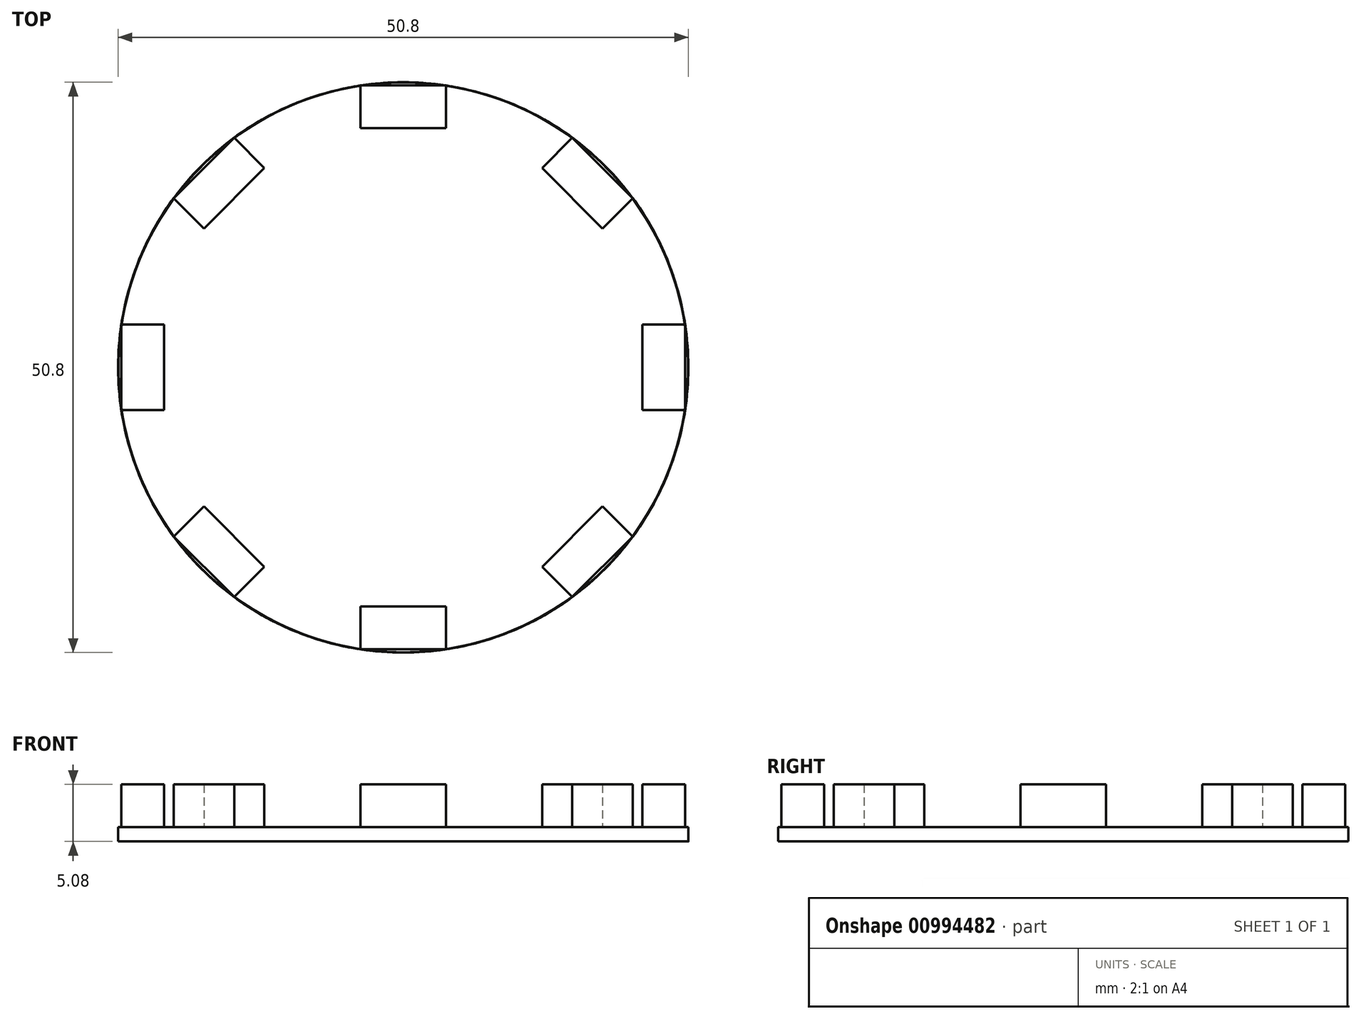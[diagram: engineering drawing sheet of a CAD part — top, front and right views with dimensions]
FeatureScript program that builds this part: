
annotation { "Feature Type Name" : "Feature", "Feature Type Description" : "" }
export const myFeature = defineFeature(function(context is Context, id is Id, definition is map)
    precondition{}
    {
        {
            var Q0;
            Q0=qCreatedBy(makeId("Top.planeOp"),FACE);
            var sketch = newSketch(context, id + "F0", { "sketchPlane" : qUnion([Q0])});
            skCircle(sketch, "E0", {"center": v(0, 0) * mm, "radius": 25.4 * mm});
            skSolve(sketch);
        }
        {
            var Q0;
            Q0 = qSketchRegion(id + "F0", true);
            extrude(context, id + "F1", {"entities" : qUnion([Q0]), "depth" : 1.27 * mm, "offsetDistance" : 25.4 * mm});
        }
        {
            var Q0;
            Q0=qCreatedBy(makeId("Top.planeOp"),FACE);
            var sketch = newSketch(context, id + "F2", { "sketchPlane" : qUnion([Q0])});
            skLineSegment(sketch, "E1.bottom", {"start": v(-25.11, 3.81) * mm, "end": v(-21.3, 3.81) * mm});
            skLineSegment(sketch, "E1.top", {"start": v(-25.11, -3.81) * mm, "end": v(-21.3, -3.81) * mm});
            skLineSegment(sketch, "E1.left", {"start": v(-25.11, 3.81) * mm, "end": v(-25.11, -3.81) * mm});
            skLineSegment(sketch, "E1.right", {"start": v(-21.3, 3.81) * mm, "end": v(-21.3, -3.81) * mm});
            skSolve(sketch);
        }
        {
            var Q0;
            Q0 = qSketchRegion(id + "F2", true);
            extrude(context, id + "F3", {"entities" : qUnion([Q0]), "operationType" : NewBodyOperationType.ADD, "depth" : 5.08 * mm, "offsetDistance" : 25.4 * mm});
        }
        {
            var Q0;
            Q0=makeQuery(id+"F1.opExtrude","SWEPT_BODY",BODY,{"disambiguationData":[OSD([sQuery(id+"F0.wireOp",EDGE,"E0")])]});
            var Q1;
            Q1=makeQuery(id+"F3.boolean.opBoolean","SPLIT",EDGE,{"disambiguationData":[OD(1.0)],"derivedFrom":makeQuery(id+"F1.opExtrude","CAP_EDGE",EDGE,{"disambiguationData":[OSD([sQuery(id+"F0.wireOp",EDGE,"E0")])],"isStart":false})});
            circularPattern(context, id + "F4", {"entities" : qUnion([Q0]), "axis" : qUnion([Q1]), "angle" : 360 * degree, "instanceCount" : 8, "equalSpace" : true});
        }
    });
